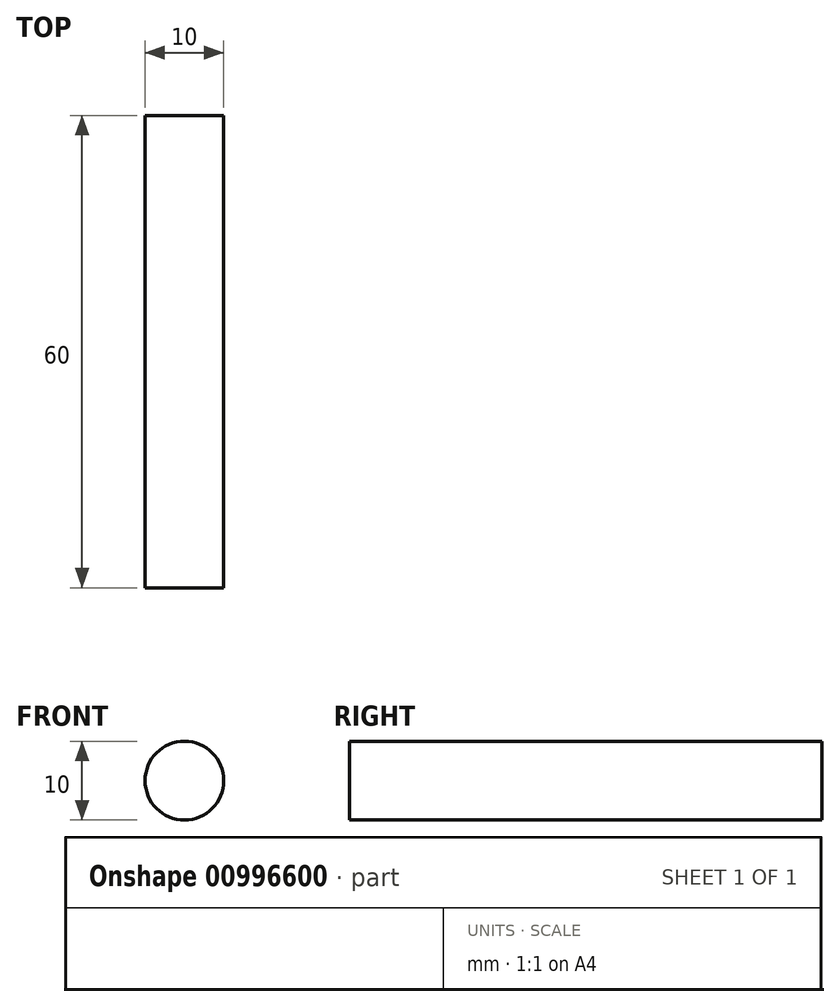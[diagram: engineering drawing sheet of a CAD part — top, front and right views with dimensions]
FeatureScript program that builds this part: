
annotation { "Feature Type Name" : "Feature", "Feature Type Description" : "" }
export const myFeature = defineFeature(function(context is Context, id is Id, definition is map)
    precondition{}
    {
        {
            var Q0;
            Q0=qCreatedBy(makeId("Front.planeOp"),FACE);
            var sketch = newSketch(context, id + "F0", { "sketchPlane" : qUnion([Q0])});
            skCircle(sketch, "E0", {"center": v(0, 0) * mm, "radius": 5 * mm});
            skSolve(sketch);
        }
        {
            var Q0;
            Q0=makeQuery(id+"F0.imprint","IMPRINT",FACE,{"disambiguationData":[TD([[makeQuery(id+"F0.imprint","IMPRINT",EDGE,{"derivedFrom":sQuery(id+"F0.wireOp",EDGE,"E0")}),1.0]])]});
            extrude(context, id + "F1", {"entities" : qUnion([Q0]), "depth" : 60 * mm, "offsetDistance" : 25 * mm});
        }
    });
